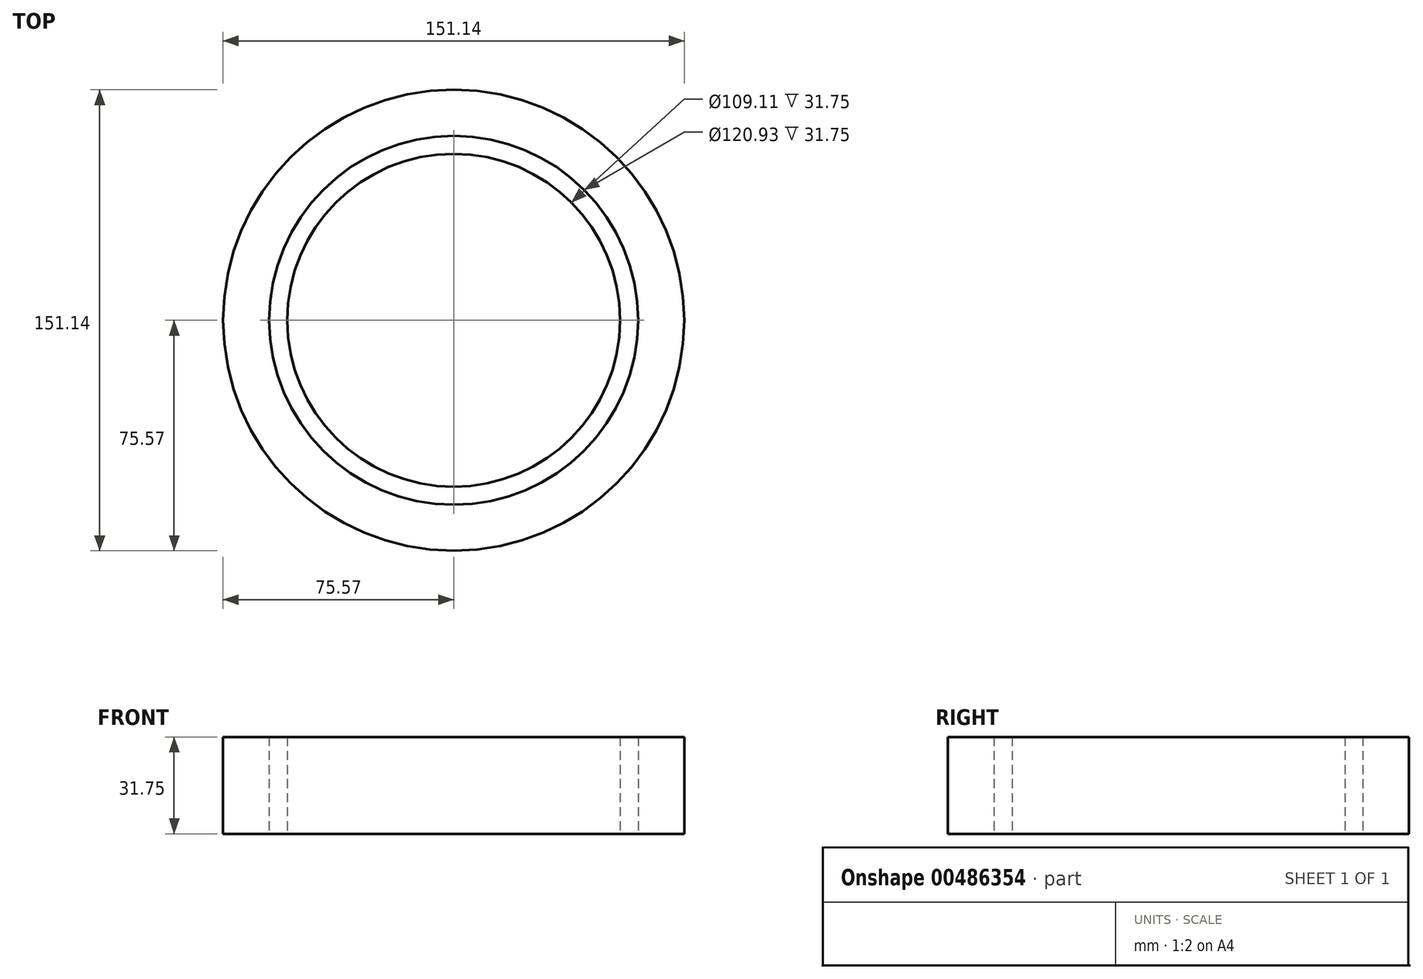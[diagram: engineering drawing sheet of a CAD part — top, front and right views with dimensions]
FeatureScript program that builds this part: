
annotation { "Feature Type Name" : "Feature", "Feature Type Description" : "" }
export const myFeature = defineFeature(function(context is Context, id is Id, definition is map)
    precondition{}
    {
        {
            var Q0;
            Q0=qCreatedBy(makeId("Top.planeOp"),FACE);
            var sketch = newSketch(context, id + "F0", { "sketchPlane" : qUnion([Q0])});
            skCircle(sketch, "E0", {"center": v(0, 0) * mm, "radius": 75.57 * mm});
            skCircle(sketch, "E1", {"center": v(0, 0) * mm, "radius": 60.46 * mm});
            skSolve(sketch);
        }
        {
            var Q0;
            Q0=makeQuery(id+"F0.imprint","IMPRINT",FACE,{"disambiguationData":[TD([[makeQuery(id+"F0.imprint","IMPRINT",EDGE,{"derivedFrom":sQuery(id+"F0.wireOp",EDGE,"E0")}),1.0]])]});
            extrude(context, id + "F1", {"entities" : qUnion([Q0]), "depth" : 31.75 * mm});
        }
        {
            var Q0;
            Q0=makeQuery(id+"F1.opExtrude","CAP_FACE",FACE,{"disambiguationData":[OSD([sQuery(id+"F0.wireOp",EDGE,"E0"),sQuery(id+"F0.wireOp",EDGE,"E1")])],"isStart":true});
            var sketch = newSketch(context, id + "F2", { "sketchPlane" : qUnion([Q0])});
            skCircle(sketch, "E2", {"center": v(0, 0) * mm, "radius": 54.55 * mm});
            skSolve(sketch);
        }
        {
            var Q0;
            Q0=makeQuery(id+"F2.imprint","IMPRINT",FACE,{"disambiguationData":[TD([[makeQuery(id+"F2.imprint","IMPRINT",EDGE,{"derivedFrom":makeQuery(id+"F1.opExtrude","CAP_EDGE",EDGE,{"disambiguationData":[OSD([sQuery(id+"F0.wireOp",EDGE,"E1")])],"isStart":true})}),-1.0]])]});
            extrude(context, id + "F3", {"entities" : qUnion([Q0]), "oppositeDirection" : true, "depth" : 31.75 * mm});
        }
    });
